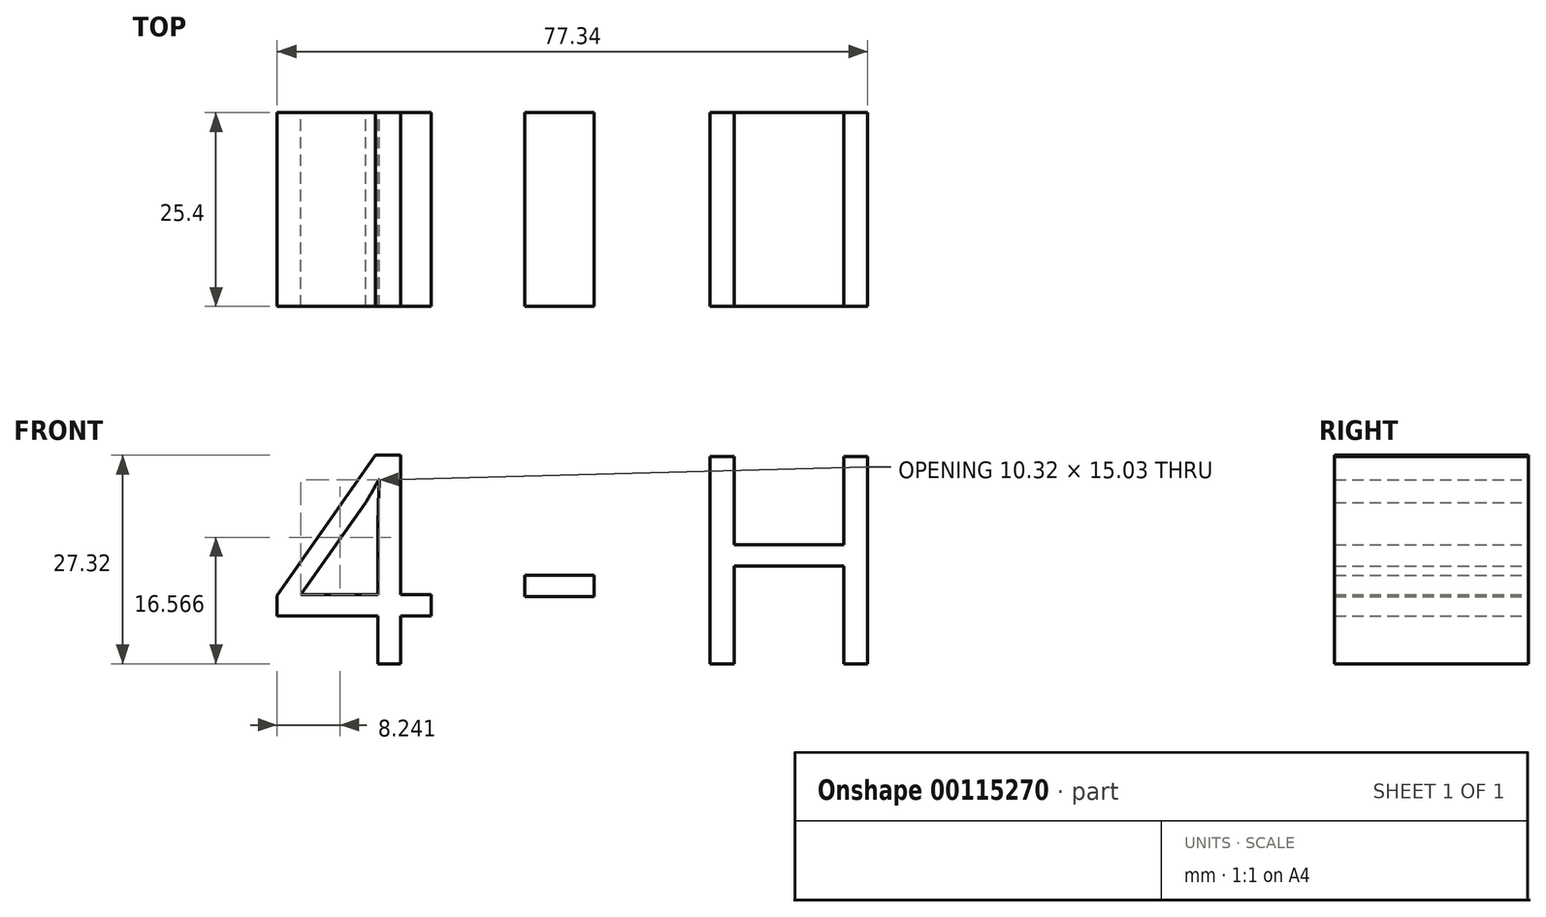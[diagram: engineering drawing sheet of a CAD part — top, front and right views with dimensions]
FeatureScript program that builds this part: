
annotation { "Feature Type Name" : "Feature", "Feature Type Description" : "" }
export const myFeature = defineFeature(function(context is Context, id is Id, definition is map)
    precondition{}
    {
        {
            var Q0;
            Q0=qCreatedBy(makeId("Front.planeOp"),FACE);
            var sketch = newSketch(context, id + "F0", { "sketchPlane" : qUnion([Q0])});
            skText(sketch, "E0", { "text": "4 - H", "fontName": "OpenSans-Regular.ttf"});
            const initialGuessF0  = {"E0": [0, 0, 1, 0, 0.0274]};
            skSetInitialGuess(sketch, initialGuessF0);
            skSolve(sketch);
        }
        {
            var Q0;
            Q0 = qSketchRegion(id + "F0", true);
            extrude(context, id + "F1", {"entities" : qUnion([Q0]), "depth" : 25.4 * mm});
        }
    });
